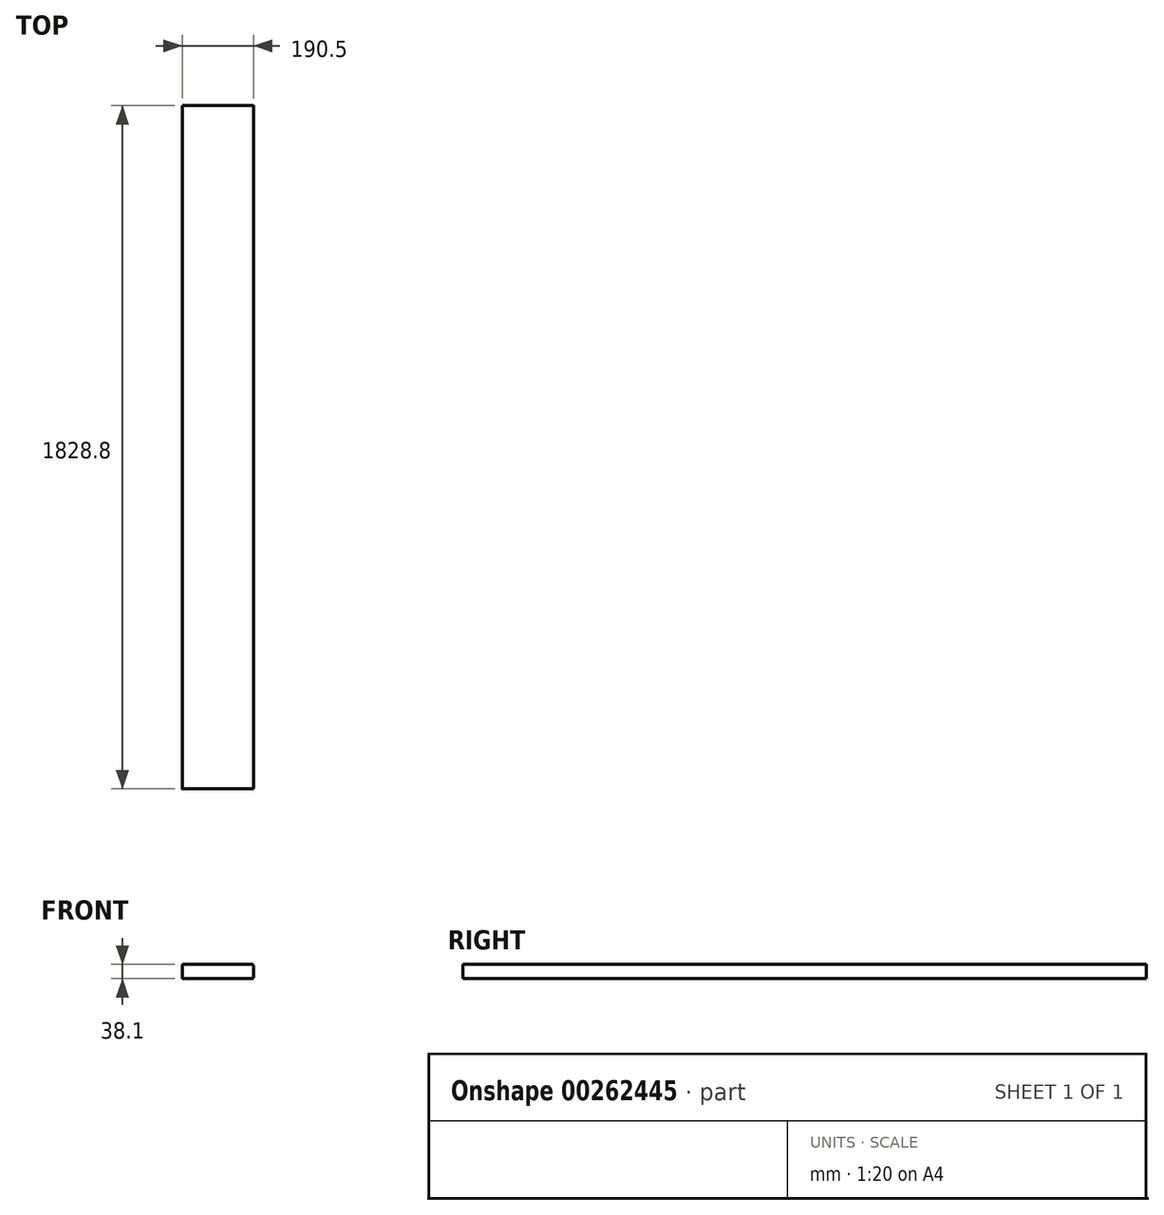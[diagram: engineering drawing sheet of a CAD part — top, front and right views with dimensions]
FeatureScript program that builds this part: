
annotation { "Feature Type Name" : "Feature", "Feature Type Description" : "" }
export const myFeature = defineFeature(function(context is Context, id is Id, definition is map)
    precondition{}
    {
        {
            var Q0;
            Q0=qCreatedBy(makeId("Front.planeOp"),FACE);
            var sketch = newSketch(context, id + "F0", { "sketchPlane" : qUnion([Q0])});
            skLineSegment(sketch, "E0.bottom", {"start": v(92.07, 19.05) * mm, "end": v(-92.08, 19.05) * mm});
            skLineSegment(sketch, "E0.top", {"start": v(92.08, -19.05) * mm, "end": v(-92.08, -19.05) * mm});
            skLineSegment(sketch, "E0.left", {"start": v(95.25, 15.87) * mm, "end": v(95.25, -15.88) * mm});
            skLineSegment(sketch, "E0.right", {"start": v(-95.25, 15.87) * mm, "end": v(-95.25, -15.88) * mm});
            skPoint(sketch, "E0.middle", {"position": v(0, 0) * mm});
            skPoint(sketch, "E1.visualSharp", {"position": v(-95.25, 19.05) * mm});
            skArc(sketch, "E1.filletArc", {"start": v(-92.08, 19.05) * mm, "mid": v(-94.32, 18.12) * mm, "end": v(-95.25, 15.87) * mm});
            skPoint(sketch, "E2.visualSharp", {"position": v(-95.25, -19.05) * mm});
            skArc(sketch, "E2.filletArc", {"start": v(-95.25, -15.88) * mm, "mid": v(-94.32, -18.12) * mm, "end": v(-92.08, -19.05) * mm});
            skPoint(sketch, "E3.visualSharp", {"position": v(95.25, 19.05) * mm});
            skArc(sketch, "E3.filletArc", {"start": v(95.25, 15.87) * mm, "mid": v(94.32, 18.12) * mm, "end": v(92.07, 19.05) * mm});
            skPoint(sketch, "E4.visualSharp", {"position": v(95.25, -19.05) * mm});
            skArc(sketch, "E4.filletArc", {"start": v(92.08, -19.05) * mm, "mid": v(94.32, -18.12) * mm, "end": v(95.25, -15.88) * mm});
            skSolve(sketch);
        }
        {
            var Q0;
            Q0=makeQuery(id+"F0.imprint","IMPRINT",FACE,{"disambiguationData":[TD([[makeQuery(id+"F0.imprint","IMPRINT",EDGE,{"derivedFrom":sQuery(id+"F0.wireOp",EDGE,"E0.bottom")}),1.0]])]});
            extrude(context, id + "F1", {"entities" : qUnion([Q0]), "depth" : 1828.8 * mm});
        }
    });
